# Revit family: Base_Cabinets-Teknion-CEBDLF_Base_Cabine_Filing_Drawers-R2023
name_source: partatom
category: Furniture
units: mm (PartAtom-declared; Revit-internal decimal feet)

## family parameters
Always vertical = Yes
Cut with Voids When Loaded = No
Enable Cutting in Views = No
OmniClass Number = 23.40.20.00
OmniClass Title = General Furniture and Specialties
Render Appearance Source = Family Geometry
Room Calculation Point = No
Shared = Yes
Work Plane-Based = No

## types (2) — shared parameters
Assembly Code = E2020200
Available Depth = 24 & 29 Inch
Drawer Style = Select one drawer style. Standard - soft close is default.
Manufacturer = Teknion
Manufacturer Fax = 416.661.4586
Part Number = CEBDLF
Product Documentation Link = https://www.teknion.com
Product Line = Base Cabinets
Product Page URL = https://www.teknion.com
S - Standard - Soft Close = Yes
Series = Expansion Casework+
Sustainability Data = https://www.teknion.com
URL = www.teknion.com
Unit Weight URL = http://www.teknion.com
Warranty = http://www.teknion.com
zero-valued in all types: Default Elevation

## per-type parameters (varying)
| type | Depth | Description | Model |
| 24" Depth | 24 " | Base Cabinet - Filing Drawers, 24" Depth, Standard - Soft Close Drawer Style | CEBDLF24__S |
| 29" Depth | 29 " | Base Cabinet - Filing Drawers, 29" Depth, Standard - Soft Close Drawer Style | CEBDLF29__S |

## geometry (parser evidence)
native form markers: Sweep x3
no freeform markers — native parametric forms only
